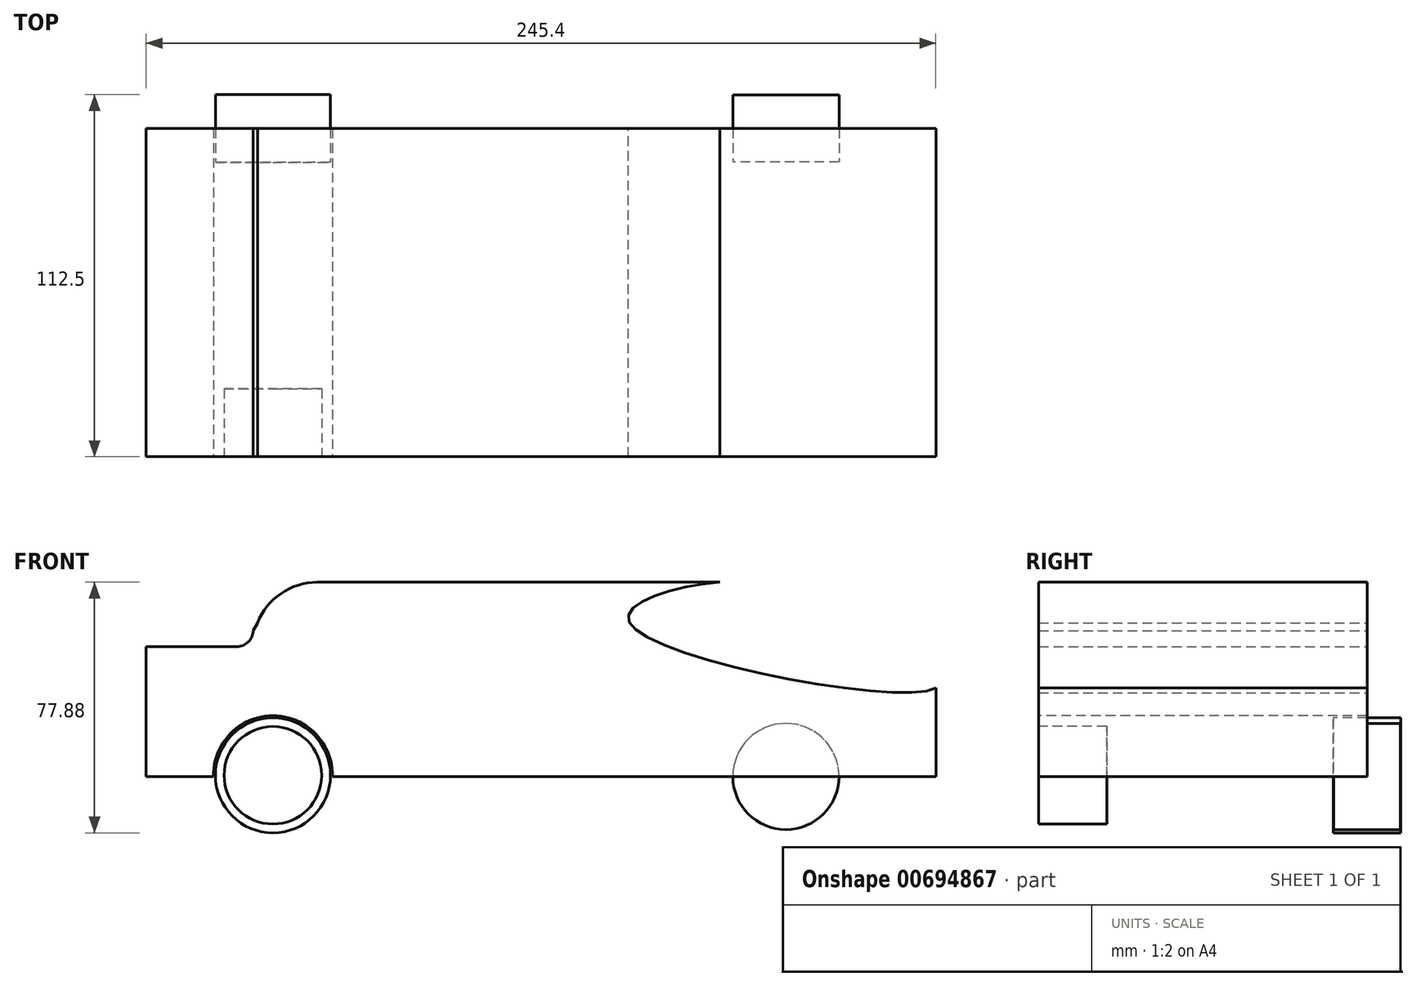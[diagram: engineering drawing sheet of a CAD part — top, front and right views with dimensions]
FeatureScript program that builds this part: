
annotation { "Feature Type Name" : "Feature", "Feature Type Description" : "" }
export const myFeature = defineFeature(function(context is Context, id is Id, definition is map)
    precondition{}
    {
        {
            var Q0;
            Q0=qCreatedBy(makeId("Front.planeOp"),FACE);
            var sketch = newSketch(context, id + "F0", { "sketchPlane" : qUnion([Q0])});
            skLineSegment(sketch, "E0.bottom", {"start": v(-122.7, 20.18) * mm, "end": v(-94.48, 20.18) * mm});
            skLineSegment(sketch, "E0.top", {"start": v(-122.7, -20.18) * mm, "end": v(122.7, -20.18) * mm});
            skLineSegment(sketch, "E0.left", {"start": v(-122.7, 20.18) * mm, "end": v(-122.7, -20.18) * mm});
            skLineSegment(sketch, "E0.right", {"start": v(122.7, 7.32) * mm, "end": v(122.7, -20.18) * mm});
            skPoint(sketch, "E0.middle", {"position": v(0, 0) * mm});
            skLineSegment(sketch, "E1.bottom", {"start": v(-69.48, 40.19) * mm, "end": v(66.54, 40.19) * mm});
            skLineSegment(sketch, "E1.right", {"start": v(89.48, 33.95) * mm, "end": v(89.48, 33.04) * mm});
            skPoint(sketch, "E1.middle", {"position": v(0, 20.18) * mm});
            skLineSegment(sketch, "E2.bottom", {"start": v(89.48, 33.04) * mm, "end": v(91.43, 33.04) * mm});
            skPoint(sketch, "E2.middle", {"position": v(105.56, 20.18) * mm});
            skPoint(sketch, "E1.top.start.orphan", {"position": v(-89.48, 0.18) * mm});
            skLineSegment(sketch, "E3.trimOffspring", {"start": v(122.7, 7.32) * mm, "end": v(129.13, 7.32) * mm});
            skPoint(sketch, "E2.left.end.orphan", {"position": v(81.98, 7.32) * mm});
            skPoint(sketch, "E4.orphan", {"position": v(81.98, 33.04) * mm});
            skPoint(sketch, "E5.orphan", {"position": v(122.7, 20.18) * mm});
            skPoint(sketch, "E6.trimOffspring.end.orphan", {"position": v(89.48, 0.18) * mm});
            skPoint(sketch, "E7.visualSharp", {"position": v(-89.48, 20.18) * mm});
            skArc(sketch, "E7.filletArc", {"start": v(-94.48, 20.18) * mm, "mid": v(-90.95, 21.65) * mm, "end": v(-89.48, 25.18) * mm});
            skPoint(sketch, "E8.visualSharp", {"position": v(-89.48, 40.19) * mm});
            skArc(sketch, "E8.filletArc", {"start": v(-69.48, 40.19) * mm, "mid": v(-80.75, 36.71) * mm, "end": v(-88.1, 27.5) * mm});
            skPoint(sketch, "E9.visualSharp", {"position": v(89.48, 40.19) * mm});
            skArc(sketch, "E9.filletArc", {"start": v(89.48, 38.04) * mm, "mid": v(88.86, 39.56) * mm, "end": v(87.34, 40.19) * mm});
            skPoint(sketch, "E10.visualSharp", {"position": v(129.13, 33.04) * mm});
            skArc(sketch, "E10.filletArc", {"start": v(129.13, 30.9) * mm, "mid": v(128.5, 32.41) * mm, "end": v(127, 33.04) * mm});
            skLineSegment(sketch, "E11", {"start": v(-89.48, 25.18) * mm, "end": v(-88.1, 27.5) * mm});
            skFitSpline(sketch, "E12", {"points": [v(55.6, 40.19) * mm, v(103.34, 26.59) * mm, v(122.7, 7.32) * mm, v(27.8, 27.16) * mm, v(55.6, 40.19) * mm]});
            skSolve(sketch);
        }
        {
            var Q0;
            Q0=makeQuery(id+"F0.imprint","IMPRINT",FACE,{"disambiguationData":[TD([[makeQuery(id+"F0.imprint","IMPRINT",EDGE,{"derivedFrom":sQuery(id+"F0.wireOp",EDGE,"E0.bottom")}),-1.0]])]});
            extrude(context, id + "F1", {"entities" : qUnion([Q0]), "endBound" : BoundingType.SYMMETRIC, "depth" : 102 * mm, "offsetDistance" : 25 * mm});
        }
        {
            var Q0;
            Q0=makeQuery(id+"F1.opExtrude","CAP_FACE",FACE,{"disambiguationData":[OSD([sQuery(id+"F0.wireOp",EDGE,"E0.bottom"),sQuery(id+"F0.wireOp",EDGE,"E0.top"),sQuery(id+"F0.wireOp",EDGE,"E0.left"),sQuery(id+"F0.wireOp",EDGE,"E0.right"),sQuery(id+"F0.wireOp",EDGE,"E1.bottom"),sQuery(id+"F0.wireOp",EDGE,"E1.right"),sQuery(id+"F0.wireOp",EDGE,"E2.bottom"),sQuery(id+"F0.wireOp",EDGE,"E2.right"),sQuery(id+"F0.wireOp",EDGE,"E3.trimOffspring"),sQuery(id+"F0.wireOp",EDGE,"E7.filletArc"),sQuery(id+"F0.wireOp",EDGE,"E8.filletArc"),sQuery(id+"F0.wireOp",EDGE,"E9.filletArc"),sQuery(id+"F0.wireOp",EDGE,"E10.filletArc"),sQuery(id+"F0.wireOp",EDGE,"E11")])],"isStart":false});
            cPlane(context, id + "F2", {"entities" : qUnion([Q0]), "cplaneType" : CPlaneType.OFFSET, "offset" : 25 * mm, "width" : 150 * mm, "height" : 150 * mm});
        }
        {
            var Q0;
            Q0=qCreatedBy(id+"F2.planeOp",FACE);
            var sketch = newSketch(context, id + "F3", { "sketchPlane" : qUnion([Q0])});
            skCircle(sketch, "E13", {"center": v(-83.3, -19.8) * mm, "radius": 18.5 * mm});
            skSolve(sketch);
        }
        {
            var Q0;
            Q0=makeQuery(id+"F3.imprint","IMPRINT",FACE,{"disambiguationData":[TD([[makeQuery(id+"F3.imprint","IMPRINT",EDGE,{"derivedFrom":sQuery(id+"F3.wireOp",EDGE,"E13")}),1.0]])]});
            extrude(context, id + "F4", {"entities" : qUnion([Q0]), "operationType" : NewBodyOperationType.REMOVE, "endBound" : BoundingType.THROUGH_ALL, "oppositeDirection" : true, "depth" : 45 * mm, "offsetDistance" : 25 * mm});
        }
        {
            var Q0;
            Q0=makeQuery(id+"F1.opExtrude","CAP_FACE",FACE,{"disambiguationData":[OSD([sQuery(id+"F0.wireOp",EDGE,"E0.bottom"),sQuery(id+"F0.wireOp",EDGE,"E0.top"),sQuery(id+"F0.wireOp",EDGE,"E0.left"),sQuery(id+"F0.wireOp",EDGE,"E0.right"),sQuery(id+"F0.wireOp",EDGE,"E1.bottom"),sQuery(id+"F0.wireOp",EDGE,"E1.right"),sQuery(id+"F0.wireOp",EDGE,"E2.bottom"),sQuery(id+"F0.wireOp",EDGE,"E7.filletArc"),sQuery(id+"F0.wireOp",EDGE,"E8.filletArc"),sQuery(id+"F0.wireOp",EDGE,"E11"),sQuery(id+"F0.wireOp",EDGE,"E12")])],"isStart":false});
            var sketch = newSketch(context, id + "F5", { "sketchPlane" : qUnion([Q0])});
            skCircle(sketch, "E14", {"center": v(-83.3, -19.8) * mm, "radius": 15.16 * mm});
            skSolve(sketch);
        }
        {
            var Q0;
            Q0=makeQuery(id+"F5.imprint","IMPRINT",FACE,{"disambiguationData":[TD([[makeQuery(id+"F5.imprint","IMPRINT",EDGE,{"derivedFrom":sQuery(id+"F5.wireOp",EDGE,"E14")}),1.0]])]});
            extrude(context, id + "F6", {"entities" : qUnion([Q0]), "oppositeDirection" : true, "depth" : 21.1 * mm, "offsetDistance" : 25 * mm});
        }
        {
            var Q0;
            Q0=makeQuery(id+"F1.opExtrude","CAP_FACE",FACE,{"disambiguationData":[OSD([sQuery(id+"F0.wireOp",EDGE,"E0.bottom"),sQuery(id+"F0.wireOp",EDGE,"E0.top"),sQuery(id+"F0.wireOp",EDGE,"E0.left"),sQuery(id+"F0.wireOp",EDGE,"E0.right"),sQuery(id+"F0.wireOp",EDGE,"E1.bottom"),sQuery(id+"F0.wireOp",EDGE,"E1.right"),sQuery(id+"F0.wireOp",EDGE,"E2.bottom"),sQuery(id+"F0.wireOp",EDGE,"E7.filletArc"),sQuery(id+"F0.wireOp",EDGE,"E8.filletArc"),sQuery(id+"F0.wireOp",EDGE,"E11"),sQuery(id+"F0.wireOp",EDGE,"E12")])],"isStart":false});
            var sketch = newSketch(context, id + "F7", { "sketchPlane" : qUnion([Q0])});
            skCircle(sketch, "E15", {"center": v(75.86, -20.18) * mm, "radius": 16.04 * mm});
            skSolve(sketch);
        }
        {
            var Q0;
            Q0=sQuery(id+"F7.wireOp",EDGE,"E15");
            extrude(context, id + "F8", {"bodyType" : ToolBodyType.SURFACE, "surfaceEntities" : qUnion([Q0]), "endBound" : BoundingType.SYMMETRIC, "oppositeDirection" : true, "depth" : 17.2 * mm, "offsetDistance" : 25 * mm});
        }
        {
            var Q0;
            Q0=makeQuery(id+"F1.opExtrude","CAP_FACE",FACE,{"disambiguationData":[OSD([sQuery(id+"F0.wireOp",EDGE,"E0.bottom"),sQuery(id+"F0.wireOp",EDGE,"E0.top"),sQuery(id+"F0.wireOp",EDGE,"E0.left"),sQuery(id+"F0.wireOp",EDGE,"E0.right"),sQuery(id+"F0.wireOp",EDGE,"E1.bottom"),sQuery(id+"F0.wireOp",EDGE,"E1.right"),sQuery(id+"F0.wireOp",EDGE,"E2.bottom"),sQuery(id+"F0.wireOp",EDGE,"E7.filletArc"),sQuery(id+"F0.wireOp",EDGE,"E8.filletArc"),sQuery(id+"F0.wireOp",EDGE,"E11"),sQuery(id+"F0.wireOp",EDGE,"E12")])],"isStart":true});
            var sketch = newSketch(context, id + "F9", { "sketchPlane" : qUnion([Q0])});
            skCircle(sketch, "E16", {"center": v(-76.1, -20.18) * mm, "radius": 16.5 * mm});
            skCircle(sketch, "E17", {"center": v(83.3, -19.8) * mm, "radius": 15.99 * mm});
            skSolve(sketch);
        }
        {
            var Q0;
            {var subQ0=sQuery(id+"F9.wireOp",EDGE,"E16");var subQ1=sQuery(id+"F0.wireOp",EDGE,"E0.right");var subQ2=sQuery(id+"F0.wireOp",EDGE,"E0.top");var subQ3=makeQuery(id+"F4.boolean.opBoolean","SPLIT",EDGE,{"disambiguationData":[TD([makeQuery(id+"F1.opExtrude","SWEPT_FACE",FACE,{"disambiguationData":[OSD([subQ1])]})])],"derivedFrom":makeQuery(id+"F1.opExtrude","CAP_EDGE",EDGE,{"disambiguationData":[OSD([subQ2])],"isStart":true})});var subQ4=makeQuery(id+"F9.imprint","INTERSECT",VERTEX,{"disambiguationData":[OD(0.0)],"derivedFrom":[subQ3,subQ0]});Q0=makeQuery(id+"F9.imprint","IMPRINT",FACE,{"disambiguationData":[TD([[makeQuery(id+"F9.imprint","IMPRINT",EDGE,{"disambiguationData":[TD([[subQ4,1.0]])],"derivedFrom":subQ0}),1.0]])]});}
            var Q1;
            {var subQ0=sQuery(id+"F9.wireOp",EDGE,"E16");var subQ1=sQuery(id+"F0.wireOp",EDGE,"E0.right");var subQ2=sQuery(id+"F0.wireOp",EDGE,"E0.top");var subQ3=makeQuery(id+"F4.boolean.opBoolean","SPLIT",EDGE,{"disambiguationData":[TD([makeQuery(id+"F1.opExtrude","SWEPT_FACE",FACE,{"disambiguationData":[OSD([subQ1])]})])],"derivedFrom":makeQuery(id+"F1.opExtrude","CAP_EDGE",EDGE,{"disambiguationData":[OSD([subQ2])],"isStart":true})});var subQ4=makeQuery(id+"F9.imprint","INTERSECT",VERTEX,{"disambiguationData":[OD(0.0)],"derivedFrom":[subQ3,subQ0]});Q1=makeQuery(id+"F9.imprint","IMPRINT",FACE,{"disambiguationData":[TD([[makeQuery(id+"F9.imprint","IMPRINT",EDGE,{"disambiguationData":[TD([[subQ4,-1.0]])],"derivedFrom":subQ0}),1.0]])]});}
            extrude(context, id + "F10", {"entities" : qUnion([Q0, Q1]), "operationType" : NewBodyOperationType.ADD, "endBound" : BoundingType.SYMMETRIC, "depth" : 20.8 * mm, "offsetDistance" : 25 * mm});
        }
        {
            var Q0;
            Q0=makeQuery(id+"F10.boolean.opBoolean","MERGE",FACE,{"derivedFrom":[makeQuery(id+"F1.opExtrude","CAP_FACE",FACE,{"disambiguationData":[OSD([sQuery(id+"F0.wireOp",EDGE,"E0.bottom"),sQuery(id+"F0.wireOp",EDGE,"E0.top"),sQuery(id+"F0.wireOp",EDGE,"E0.left"),sQuery(id+"F0.wireOp",EDGE,"E0.right"),sQuery(id+"F0.wireOp",EDGE,"E1.bottom"),sQuery(id+"F0.wireOp",EDGE,"E1.right"),sQuery(id+"F0.wireOp",EDGE,"E2.bottom"),sQuery(id+"F0.wireOp",EDGE,"E7.filletArc"),sQuery(id+"F0.wireOp",EDGE,"E8.filletArc"),sQuery(id+"F0.wireOp",EDGE,"E11"),sQuery(id+"F0.wireOp",EDGE,"E12")])],"isStart":true}),makeQuery(id+"F10.opExtrude","CAP_FACE",FACE,{"disambiguationData":[OSD([sQuery(id+"F9.wireOp",EDGE,"E16")])],"isStart":true})]});
            var sketch = newSketch(context, id + "F11", { "sketchPlane" : qUnion([Q0])});
            skCircle(sketch, "E18", {"center": v(83.3, -19.8) * mm, "radius": 17.9 * mm});
            skSolve(sketch);
        }
        {
            var Q0;
            Q0=makeQuery(id+"F11.imprint","IMPRINT",FACE,{"disambiguationData":[TD([[makeQuery(id+"F11.imprint","IMPRINT",EDGE,{"derivedFrom":sQuery(id+"F11.wireOp",EDGE,"E18")}),1.0]])]});
            extrude(context, id + "F12", {"entities" : qUnion([Q0]), "endBound" : BoundingType.SYMMETRIC, "depth" : 21 * mm, "offsetDistance" : 25 * mm});
        }
    });
